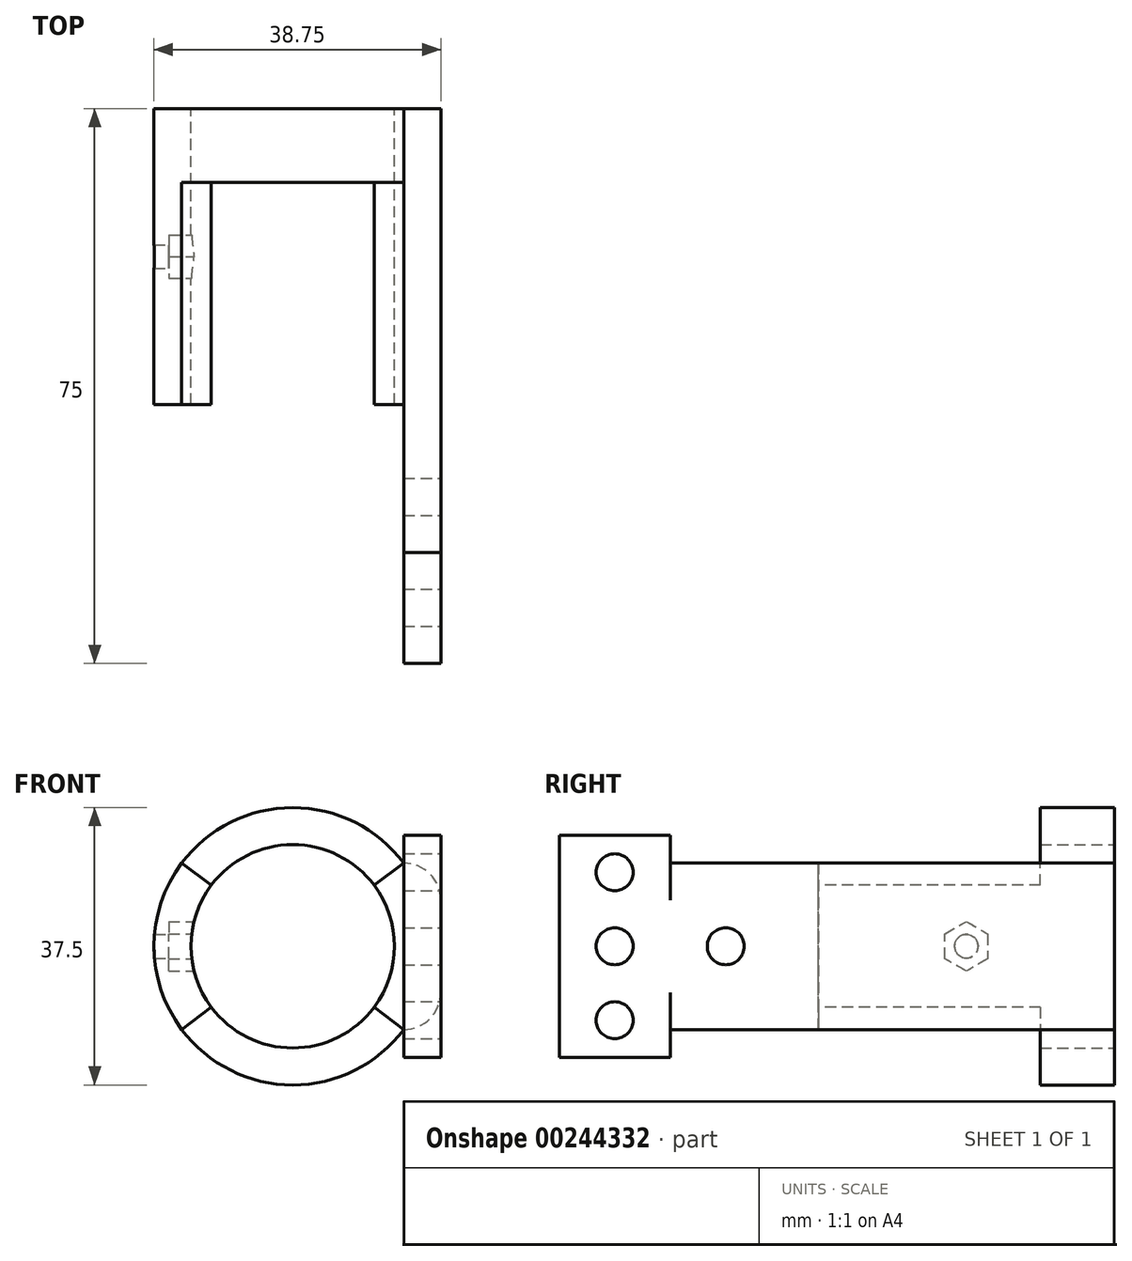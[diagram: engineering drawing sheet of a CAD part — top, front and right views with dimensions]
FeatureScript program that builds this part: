
annotation { "Feature Type Name" : "Feature", "Feature Type Description" : "" }
export const myFeature = defineFeature(function(context is Context, id is Id, definition is map)
    precondition{}
    {
        {
            var Q0;
            Q0=qCreatedBy(makeId("Front.planeOp"),FACE);
            var sketch = newSketch(context, id + "F0", { "sketchPlane" : qUnion([Q0])});
            skCircle(sketch, "E0", {"center": v(0, 0) * mm, "radius": 13.75 * mm});
            skCircle(sketch, "E1", {"center": v(0, 0) * mm, "radius": 18.75 * mm});
            skSolve(sketch);
        }
        {
            var Q0;
            Q0=qSketchRegion(id+"F0",true);
            extrude(context, id + "F1", {"entities" : qUnion([Q0]), "depth" : 40 * mm});
        }
        {
            var Q0;
            Q0=makeQuery(id+"F1.opExtrude","CAP_FACE",FACE,{"disambiguationData":[OSD([sQuery(id+"F0.wireOp",EDGE,"E0"),sQuery(id+"F0.wireOp",EDGE,"E1")])],"isStart":false});
            var sketch = newSketch(context, id + "F2", { "sketchPlane" : qUnion([Q0])});
            skArc(sketch, "E2.0", {"start": v(11, 8.25) * mm, "mid": v(0, 13.75) * mm, "end": v(-11, 8.25) * mm});
            skArc(sketch, "E3.0", {"start": v(15, 11.25) * mm, "mid": v(0, 18.75) * mm, "end": v(-15, 11.25) * mm});
            skLineSegment(sketch, "E4", {"start": v(-11, 8.25) * mm, "end": v(-15, 11.25) * mm});
            skLineSegment(sketch, "E5", {"start": v(11, 8.25) * mm, "end": v(15, 11.25) * mm});
            skLineSegment(sketch, "E6", {"start": v(-11, 8.25) * mm, "end": v(11, 8.25) * mm, "construction": true});
            skLineSegment(sketch, "E7", {"start": v(-36.94, 0) * mm, "end": v(98.5, 0) * mm, "construction": true});
            skLineSegment(sketch, "E8.MirrorCS", {"start": v(11, -8.25) * mm, "end": v(15, -11.25) * mm});
            skLineSegment(sketch, "E9.MirrorCS", {"start": v(-11, -8.25) * mm, "end": v(-15, -11.25) * mm});
            skArc(sketch, "E10.MirrorCS", {"start": v(15, -11.25) * mm, "mid": v(0, -18.75) * mm, "end": v(-15, -11.25) * mm});
            skArc(sketch, "E11.MirrorCS", {"start": v(11, -8.25) * mm, "mid": v(0, -13.75) * mm, "end": v(-11, -8.25) * mm});
            skSolve(sketch);
        }
        {
            var Q0;
            Q0=qSketchRegion(id+"F2",true);
            extrude(context, id + "F3", {"entities" : qUnion([Q0]), "operationType" : NewBodyOperationType.REMOVE, "oppositeDirection" : true, "depth" : 30 * mm});
        }
        {
            var Q0;
            Q0=qCreatedBy(makeId("Right.planeOp"),FACE);
            var sketch = newSketch(context, id + "F4", { "sketchPlane" : qUnion([Q0])});
            skLineSegment(sketch, "E12", {"start": v(-20, 106.95) * mm, "end": v(-20, -100.29) * mm, "construction": true});
            skLineSegment(sketch, "E13", {"start": v(-88.53, 0) * mm, "end": v(41.2, 0) * mm, "construction": true});
            skCircle(sketch, "E14", {"center": v(-20, 0) * mm, "radius": 1.6 * mm});
            skCircle(sketch, "E15.cCircle", {"center": v(-20, 0) * mm, "radius": 2.9 * mm, "construction": true});
            skLineSegment(sketch, "E15.0", {"start": v(-22.9, -1.67) * mm, "end": v(-22.9, 1.67) * mm});
            skLineSegment(sketch, "E15.1", {"start": v(-22.9, 1.67) * mm, "end": v(-20, 3.35) * mm});
            skLineSegment(sketch, "E15.2", {"start": v(-20, 3.35) * mm, "end": v(-17.1, 1.67) * mm});
            skLineSegment(sketch, "E15.3", {"start": v(-17.1, 1.67) * mm, "end": v(-17.1, -1.67) * mm});
            skLineSegment(sketch, "E15.4", {"start": v(-17.1, -1.67) * mm, "end": v(-20, -3.35) * mm});
            skLineSegment(sketch, "E15.5", {"start": v(-20, -3.35) * mm, "end": v(-22.9, -1.67) * mm});
            skPoint(sketch, "E15.0.midPoint", {"position": v(-22.9, 0) * mm});
            skSolve(sketch);
        }
        {
            var Q0;
            Q0=makeQuery(id+"F4.imprint","IMPRINT",FACE,{"disambiguationData":[TD([[makeQuery(id+"F4.imprint","IMPRINT",EDGE,{"derivedFrom":sQuery(id+"F4.wireOp",EDGE,"E14")}),1.0]])]});
            var Q1;
            Q1=makeQuery(id+"Fqsz4co2HmxNiW1_1.opFillet","SPLIT",FACE,{"disambiguationData":[OD(0.0)],"derivedFrom":makeQuery(id+"F1.opExtrude","SWEPT_FACE",FACE,{"disambiguationData":[OSD([sQuery(id+"F0.wireOp",EDGE,"E1")])]})});
            extrude(context, id + "F5", {"entities" : qUnion([Q0]), "operationType" : NewBodyOperationType.REMOVE, "endBound" : BoundingType.UP_TO_SURFACE, "oppositeDirection" : true, "endBoundEntityFace" : qUnion([Q1]), "depth" : 25 * mm});
        }
        {
            var Q0;
            Q0=makeQuery(id+"F4.imprint","IMPRINT",FACE,{"disambiguationData":[TD([[makeQuery(id+"F4.imprint","IMPRINT",EDGE,{"derivedFrom":sQuery(id+"F4.wireOp",EDGE,"E14")}),-1.0]])]});
            extrude(context, id + "F6", {"entities" : qUnion([Q0]), "operationType" : NewBodyOperationType.REMOVE, "oppositeDirection" : true, "depth" : 16.75 * mm});
        }
        {
            var Q0;
            Q0=qCreatedBy(makeId("Right.planeOp"),FACE);
            cPlane(context, id + "F7", {"entities" : qUnion([Q0]), "cplaneType" : CPlaneType.OFFSET, "offset" : 20 * mm, "width" : 150 * mm, "height" : 150 * mm});
        }
        {
            var Q0;
            Q0=qCreatedBy(id+"F7.planeOp",FACE);
            var sketch = newSketch(context, id + "F8", { "sketchPlane" : qUnion([Q0])});
            skLineSegment(sketch, "E16.bottom", {"start": v(-60, 11.25) * mm, "end": v(0, 11.25) * mm});
            skLineSegment(sketch, "E16.top", {"start": v(-60, -11.25) * mm, "end": v(0, -11.25) * mm});
            skLineSegment(sketch, "E16.right", {"start": v(0, 11.25) * mm, "end": v(0, -11.25) * mm});
            skLineSegment(sketch, "E17.bottom", {"start": v(-75, 15) * mm, "end": v(-60, 15) * mm});
            skLineSegment(sketch, "E17.top", {"start": v(-75, -15) * mm, "end": v(-60, -15) * mm});
            skLineSegment(sketch, "E17.left", {"start": v(-75, 15) * mm, "end": v(-75, -15) * mm});
            skLineSegment(sketch, "E17.right", {"start": v(-60, 15) * mm, "end": v(-60, 11.25) * mm});
            skLineSegment(sketch, "E18.trimOffspring", {"start": v(-60, -11.25) * mm, "end": v(-60, -15) * mm});
            skLineSegment(sketch, "E19", {"start": v(-139.42, 0) * mm, "end": v(30.7, 0) * mm, "construction": true});
            skLineSegment(sketch, "E20", {"start": v(-67.5, 15) * mm, "end": v(-67.5, -15) * mm, "construction": true});
            skCircle(sketch, "E21", {"center": v(-67.5, 0) * mm, "radius": 2.5 * mm});
            skCircle(sketch, "E22", {"center": v(-67.5, 10) * mm, "radius": 2.5 * mm});
            skCircle(sketch, "E23", {"center": v(-67.5, -10) * mm, "radius": 2.5 * mm});
            skCircle(sketch, "E24", {"center": v(-52.5, 0) * mm, "radius": 2.5 * mm});
            skSolve(sketch);
        }
        {
            var Q0;
            Q0 = qSketchRegion(id + "F8", true);
            extrude(context, id + "F9", {"entities" : qUnion([Q0]), "operationType" : NewBodyOperationType.ADD, "oppositeDirection" : true, "depth" : 5 * mm});
        }
        {
            var Q0;
            Q0=makeQuery(id+"F9.opExtrude","CAP_EDGE",EDGE,{"disambiguationData":[OSD([sQuery(id+"F8.wireOp",EDGE,"E16.bottom")])],"isStart":true});
            var Q1;
            Q1=makeQuery(id+"F9.opExtrude","CAP_EDGE",EDGE,{"disambiguationData":[OSD([sQuery(id+"F8.wireOp",EDGE,"E16.top")])],"isStart":true});
            fillet(context, id + "F10", {"entities" : qUnion([Q0, Q1]), "radius" : 5 * mm, "tangentPropagation" : true, "allowEdgeOverflow" : false});
        }
    });
